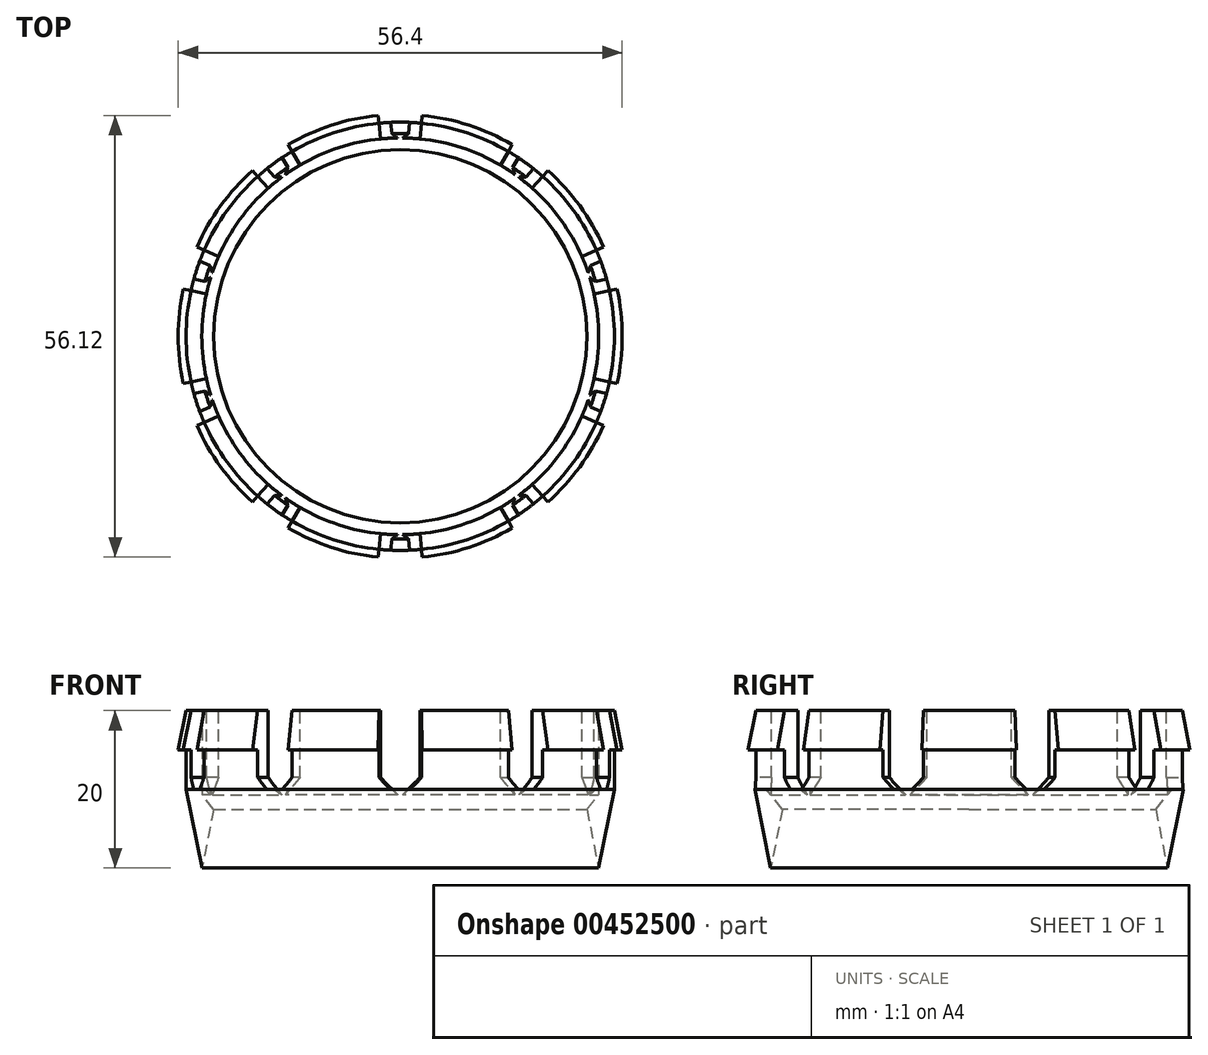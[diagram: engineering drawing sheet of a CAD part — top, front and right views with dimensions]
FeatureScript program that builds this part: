
annotation { "Feature Type Name" : "Feature", "Feature Type Description" : "" }
export const myFeature = defineFeature(function(context is Context, id is Id, definition is map)
    precondition{}
    {
        {
            var Q0;
            Q0=qCreatedBy(makeId("Front.planeOp"),FACE);
            var sketch = newSketch(context, id + "F0", { "sketchPlane" : qUnion([Q0])});
            skLineSegment(sketch, "E0", {"start": v(-25.2, 10) * mm, "end": v(-25.2, -10) * mm});
            skLineSegment(sketch, "E1", {"start": v(-25.2, -10) * mm, "end": v(-27.2, 0) * mm});
            skLineSegment(sketch, "E2", {"start": v(-25.2, -10) * mm, "end": v(-23.2, 0) * mm});
            skLineSegment(sketch, "E3", {"start": v(-23.2, 0) * mm, "end": v(-25.2, 0) * mm});
            skLineSegment(sketch, "E4", {"start": v(-27.2, 0) * mm, "end": v(-27.2, 10) * mm});
            skLineSegment(sketch, "E5", {"start": v(-27.2, 10) * mm, "end": v(-28.2, 5) * mm});
            skLineSegment(sketch, "E6", {"start": v(-28.2, 5) * mm, "end": v(-27.2, 5) * mm});
            skLineSegment(sketch, "E7", {"start": v(-27.2, 10) * mm, "end": v(-25.2, 10) * mm});
            skSolve(sketch);
        }
        {
            var Q0;
            Q0=qCreatedBy(makeId("Top.planeOp"),FACE);
            var sketch = newSketch(context, id + "F1", { "sketchPlane" : qUnion([Q0])});
            skCircle(sketch, "E8", {"center": v(0, 0) * mm, "radius": 32.32 * mm});
            skSolve(sketch);
        }
        {
            var Q0;
            Q0 = qSketchRegion(id + "F0", true);
            var Q1;
            Q1=sQuery(id+"F1.wireOp",EDGE,"E8");
            revolve(context, id + "F2", {"entities" : qUnion([Q0]), "axis" : qUnion([Q1]), "revolveType" : RevolveType.FULL});
        }
        {
            var Q0;
            Q0=makeQuery(id+"F2.opRevolve","SWEPT_FACE",FACE,{"disambiguationData":[OSD([sQuery(id+"F0.wireOp",EDGE,"E7")])]});
            var sketch = newSketch(context, id + "F3", { "sketchPlane" : qUnion([Q0])});
            skCircle(sketch, "E9.0", {"center": v(0, 0) * mm, "radius": 25.2 * mm, "construction": true});
            skCircle(sketch, "E10.0", {"center": v(0, 0) * mm, "radius": 28.2 * mm, "construction": true});
            skLineSegment(sketch, "E11", {"start": v(0, 0) * mm, "end": v(0, 37.47) * mm, "construction": true});
            skLineSegment(sketch, "E12", {"start": v(-2.5, 25.08) * mm, "end": v(-2.8, 28.06) * mm});
            skLineSegment(sketch, "E13", {"start": v(-2.5, 25.08) * mm, "end": v(18.62, 27.18) * mm, "construction": true});
            skLineSegment(sketch, "E14.MirrorCS", {"start": v(2.5, 25.08) * mm, "end": v(2.8, 28.06) * mm});
            skArc(sketch, "E15", {"start": v(-2.8, 28.06) * mm, "mid": v(0, 28.2) * mm, "end": v(2.8, 28.06) * mm});
            skArc(sketch, "E16", {"start": v(-2.5, 25.08) * mm, "mid": v(0, 25.2) * mm, "end": v(2.5, 25.08) * mm});
            skLineSegment(sketch, "E17.1.0", {"start": v(-12.72, 21.76) * mm, "end": v(-14.23, 24.35) * mm});
            skLineSegment(sketch, "E17.1.1", {"start": v(-16.76, 18.82) * mm, "end": v(-18.76, 21.06) * mm});
            skArc(sketch, "E17.1.2", {"start": v(-18.76, 21.06) * mm, "mid": v(-16.58, 22.81) * mm, "end": v(-14.23, 24.35) * mm});
            skArc(sketch, "E17.1.3", {"start": v(-16.76, 18.82) * mm, "mid": v(-14.81, 20.39) * mm, "end": v(-12.72, 21.76) * mm});
            skLineSegment(sketch, "E17.2.0", {"start": v(-23.08, 10.13) * mm, "end": v(-25.82, 11.33) * mm});
            skLineSegment(sketch, "E17.2.1", {"start": v(-24.62, 5.37) * mm, "end": v(-27.55, 6.01) * mm});
            skArc(sketch, "E17.2.2", {"start": v(-27.55, 6.01) * mm, "mid": v(-26.82, 8.71) * mm, "end": v(-25.82, 11.33) * mm});
            skArc(sketch, "E17.2.3", {"start": v(-24.62, 5.37) * mm, "mid": v(-23.97, 7.79) * mm, "end": v(-23.08, 10.13) * mm});
            skLineSegment(sketch, "E17.3.0", {"start": v(-24.62, -5.37) * mm, "end": v(-27.55, -6.01) * mm});
            skLineSegment(sketch, "E17.3.1", {"start": v(-23.08, -10.13) * mm, "end": v(-25.82, -11.33) * mm});
            skArc(sketch, "E17.3.2", {"start": v(-25.82, -11.33) * mm, "mid": v(-26.82, -8.71) * mm, "end": v(-27.55, -6.01) * mm});
            skArc(sketch, "E17.3.3", {"start": v(-23.08, -10.13) * mm, "mid": v(-23.97, -7.79) * mm, "end": v(-24.62, -5.37) * mm});
            skLineSegment(sketch, "E17.4.0", {"start": v(-16.76, -18.82) * mm, "end": v(-18.76, -21.06) * mm});
            skLineSegment(sketch, "E17.4.1", {"start": v(-12.72, -21.76) * mm, "end": v(-14.23, -24.35) * mm});
            skArc(sketch, "E17.4.2", {"start": v(-14.23, -24.35) * mm, "mid": v(-16.58, -22.81) * mm, "end": v(-18.76, -21.06) * mm});
            skArc(sketch, "E17.4.3", {"start": v(-12.72, -21.76) * mm, "mid": v(-14.81, -20.39) * mm, "end": v(-16.76, -18.82) * mm});
            skLineSegment(sketch, "E17.5.0", {"start": v(-2.5, -25.08) * mm, "end": v(-2.8, -28.06) * mm});
            skLineSegment(sketch, "E17.5.1", {"start": v(2.5, -25.08) * mm, "end": v(2.8, -28.06) * mm});
            skArc(sketch, "E17.5.2", {"start": v(2.8, -28.06) * mm, "mid": v(0, -28.2) * mm, "end": v(-2.8, -28.06) * mm});
            skArc(sketch, "E17.5.3", {"start": v(2.5, -25.08) * mm, "mid": v(0, -25.2) * mm, "end": v(-2.5, -25.08) * mm});
            skLineSegment(sketch, "E17.6.0", {"start": v(12.72, -21.76) * mm, "end": v(14.23, -24.35) * mm});
            skLineSegment(sketch, "E17.6.1", {"start": v(16.76, -18.82) * mm, "end": v(18.76, -21.06) * mm});
            skArc(sketch, "E17.6.2", {"start": v(18.76, -21.06) * mm, "mid": v(16.58, -22.81) * mm, "end": v(14.23, -24.35) * mm});
            skArc(sketch, "E17.6.3", {"start": v(16.76, -18.82) * mm, "mid": v(14.81, -20.39) * mm, "end": v(12.72, -21.76) * mm});
            skLineSegment(sketch, "E17.7.0", {"start": v(23.08, -10.13) * mm, "end": v(25.82, -11.33) * mm});
            skLineSegment(sketch, "E17.7.1", {"start": v(24.62, -5.37) * mm, "end": v(27.55, -6.01) * mm});
            skArc(sketch, "E17.7.2", {"start": v(27.55, -6.01) * mm, "mid": v(26.82, -8.71) * mm, "end": v(25.82, -11.33) * mm});
            skArc(sketch, "E17.7.3", {"start": v(24.62, -5.37) * mm, "mid": v(23.97, -7.79) * mm, "end": v(23.08, -10.13) * mm});
            skLineSegment(sketch, "E17.8.0", {"start": v(24.62, 5.37) * mm, "end": v(27.55, 6.01) * mm});
            skLineSegment(sketch, "E17.8.1", {"start": v(23.08, 10.13) * mm, "end": v(25.82, 11.33) * mm});
            skArc(sketch, "E17.8.2", {"start": v(25.82, 11.33) * mm, "mid": v(26.82, 8.71) * mm, "end": v(27.55, 6.01) * mm});
            skArc(sketch, "E17.8.3", {"start": v(23.08, 10.13) * mm, "mid": v(23.97, 7.79) * mm, "end": v(24.62, 5.37) * mm});
            skLineSegment(sketch, "E17.9.0", {"start": v(16.76, 18.82) * mm, "end": v(18.76, 21.06) * mm});
            skLineSegment(sketch, "E17.9.1", {"start": v(12.72, 21.76) * mm, "end": v(14.23, 24.35) * mm});
            skArc(sketch, "E17.9.2", {"start": v(14.23, 24.35) * mm, "mid": v(16.58, 22.81) * mm, "end": v(18.76, 21.06) * mm});
            skArc(sketch, "E17.9.3", {"start": v(12.72, 21.76) * mm, "mid": v(14.81, 20.39) * mm, "end": v(16.76, 18.82) * mm});
            skSolve(sketch);
        }
        {
            var Q0;
            Q0 = qSketchRegion(id + "F3", true);
            var Q1;
            Q1=makeQuery(id+"F2.opRevolve","SWEPT_FACE",FACE,{"disambiguationData":[OSD([sQuery(id+"F0.wireOp",EDGE,"E3")])]});
            extrude(context, id + "F4", {"entities" : qUnion([Q0]), "operationType" : NewBodyOperationType.REMOVE, "endBound" : BoundingType.UP_TO_SURFACE, "oppositeDirection" : true, "endBoundEntityFace" : qUnion([Q1]), "depth" : 25 * mm});
        }
        {
            var Q0;
            Q0=makeQuery(id+"F4.boolean.opBoolean","COPY",EDGE,{"derivedFrom":makeQuery(id+"F4.opExtrude","CAP_EDGE",EDGE,{"disambiguationData":[OSD([sQuery(id+"F3.wireOp",EDGE,"E17.4.0")])],"isStart":false})});
            var Q1;
            Q1=makeQuery(id+"F4.boolean.opBoolean","COPY",EDGE,{"derivedFrom":makeQuery(id+"F4.opExtrude","CAP_EDGE",EDGE,{"disambiguationData":[OSD([sQuery(id+"F3.wireOp",EDGE,"E17.4.1")])],"isStart":false})});
            var Q2;
            Q2=makeQuery(id+"F4.boolean.opBoolean","COPY",EDGE,{"derivedFrom":makeQuery(id+"F4.opExtrude","CAP_EDGE",EDGE,{"disambiguationData":[OSD([sQuery(id+"F3.wireOp",EDGE,"E17.3.1")])],"isStart":false})});
            var Q3;
            Q3=makeQuery(id+"F4.boolean.opBoolean","COPY",EDGE,{"derivedFrom":makeQuery(id+"F4.opExtrude","CAP_EDGE",EDGE,{"disambiguationData":[OSD([sQuery(id+"F3.wireOp",EDGE,"E17.3.0")])],"isStart":false})});
            var Q4;
            Q4=makeQuery(id+"F4.boolean.opBoolean","COPY",EDGE,{"derivedFrom":makeQuery(id+"F4.opExtrude","CAP_EDGE",EDGE,{"disambiguationData":[OSD([sQuery(id+"F3.wireOp",EDGE,"E17.2.0")])],"isStart":false})});
            var Q5;
            Q5=makeQuery(id+"F4.boolean.opBoolean","COPY",EDGE,{"derivedFrom":makeQuery(id+"F4.opExtrude","CAP_EDGE",EDGE,{"disambiguationData":[OSD([sQuery(id+"F3.wireOp",EDGE,"E17.2.1")])],"isStart":false})});
            var Q6;
            Q6=makeQuery(id+"F4.boolean.opBoolean","COPY",EDGE,{"derivedFrom":makeQuery(id+"F4.opExtrude","CAP_EDGE",EDGE,{"disambiguationData":[OSD([sQuery(id+"F3.wireOp",EDGE,"E17.1.0")])],"isStart":false})});
            var Q7;
            Q7=makeQuery(id+"F4.boolean.opBoolean","COPY",EDGE,{"derivedFrom":makeQuery(id+"F4.opExtrude","CAP_EDGE",EDGE,{"disambiguationData":[OSD([sQuery(id+"F3.wireOp",EDGE,"E17.1.1")])],"isStart":false})});
            var Q8;
            Q8=makeQuery(id+"F4.boolean.opBoolean","COPY",EDGE,{"derivedFrom":makeQuery(id+"F4.opExtrude","CAP_EDGE",EDGE,{"disambiguationData":[OSD([sQuery(id+"F3.wireOp",EDGE,"E12")])],"isStart":false})});
            var Q9;
            Q9=makeQuery(id+"F4.boolean.opBoolean","COPY",EDGE,{"derivedFrom":makeQuery(id+"F4.opExtrude","CAP_EDGE",EDGE,{"disambiguationData":[OSD([sQuery(id+"F3.wireOp",EDGE,"E14.MirrorCS")])],"isStart":false})});
            var Q10;
            Q10=makeQuery(id+"F4.boolean.opBoolean","COPY",EDGE,{"derivedFrom":makeQuery(id+"F4.opExtrude","CAP_EDGE",EDGE,{"disambiguationData":[OSD([sQuery(id+"F3.wireOp",EDGE,"E17.9.1")])],"isStart":false})});
            var Q11;
            Q11=makeQuery(id+"F4.boolean.opBoolean","COPY",EDGE,{"derivedFrom":makeQuery(id+"F4.opExtrude","CAP_EDGE",EDGE,{"disambiguationData":[OSD([sQuery(id+"F3.wireOp",EDGE,"E17.8.1")])],"isStart":false})});
            var Q12;
            Q12=makeQuery(id+"F4.boolean.opBoolean","COPY",EDGE,{"derivedFrom":makeQuery(id+"F4.opExtrude","CAP_EDGE",EDGE,{"disambiguationData":[OSD([sQuery(id+"F3.wireOp",EDGE,"E17.7.1")])],"isStart":false})});
            var Q13;
            Q13=makeQuery(id+"F4.boolean.opBoolean","COPY",EDGE,{"derivedFrom":makeQuery(id+"F4.opExtrude","CAP_EDGE",EDGE,{"disambiguationData":[OSD([sQuery(id+"F3.wireOp",EDGE,"E17.6.1")])],"isStart":false})});
            var Q14;
            Q14=makeQuery(id+"F4.boolean.opBoolean","COPY",EDGE,{"derivedFrom":makeQuery(id+"F4.opExtrude","CAP_EDGE",EDGE,{"disambiguationData":[OSD([sQuery(id+"F3.wireOp",EDGE,"E17.5.1")])],"isStart":false})});
            var Q15;
            Q15=makeQuery(id+"F4.boolean.opBoolean","COPY",EDGE,{"derivedFrom":makeQuery(id+"F4.opExtrude","CAP_EDGE",EDGE,{"disambiguationData":[OSD([sQuery(id+"F3.wireOp",EDGE,"E17.5.0")])],"isStart":false})});
            var Q16;
            Q16=makeQuery(id+"F4.boolean.opBoolean","COPY",EDGE,{"derivedFrom":makeQuery(id+"F4.opExtrude","CAP_EDGE",EDGE,{"disambiguationData":[OSD([sQuery(id+"F3.wireOp",EDGE,"E17.6.0")])],"isStart":false})});
            var Q17;
            Q17=makeQuery(id+"F4.boolean.opBoolean","COPY",EDGE,{"derivedFrom":makeQuery(id+"F4.opExtrude","CAP_EDGE",EDGE,{"disambiguationData":[OSD([sQuery(id+"F3.wireOp",EDGE,"E17.7.0")])],"isStart":false})});
            var Q18;
            Q18=makeQuery(id+"F4.boolean.opBoolean","COPY",EDGE,{"derivedFrom":makeQuery(id+"F4.opExtrude","CAP_EDGE",EDGE,{"disambiguationData":[OSD([sQuery(id+"F3.wireOp",EDGE,"E17.8.0")])],"isStart":false})});
            var Q19;
            Q19=makeQuery(id+"F4.boolean.opBoolean","COPY",EDGE,{"derivedFrom":makeQuery(id+"F4.opExtrude","CAP_EDGE",EDGE,{"disambiguationData":[OSD([sQuery(id+"F3.wireOp",EDGE,"E17.9.0")])],"isStart":false})});
            chamfer(context, id + "F5", {"entities" : qUnion([Q0, Q1, Q2, Q3, Q4, Q5, Q6, Q7, Q8, Q9, Q10, Q11, Q12, Q13, Q14, Q15, Q16, Q17, Q18, Q19]), "width" : 1.5 * mm, "tangentPropagation" : true});
        }
        {
            var Q0;
            Q0=makeQuery(id+"F2.opRevolve","SWEPT_EDGE",EDGE,{"disambiguationData":[OSD([sQuery(id+"F0.wireOp",EDGE,"E2"),sQuery(id+"F0.wireOp",EDGE,"E3")])]});
            chamfer(context, id + "F6", {"entities" : qUnion([Q0]), "width" : 2.1 * mm, "tangentPropagation" : true});
        }
    });
